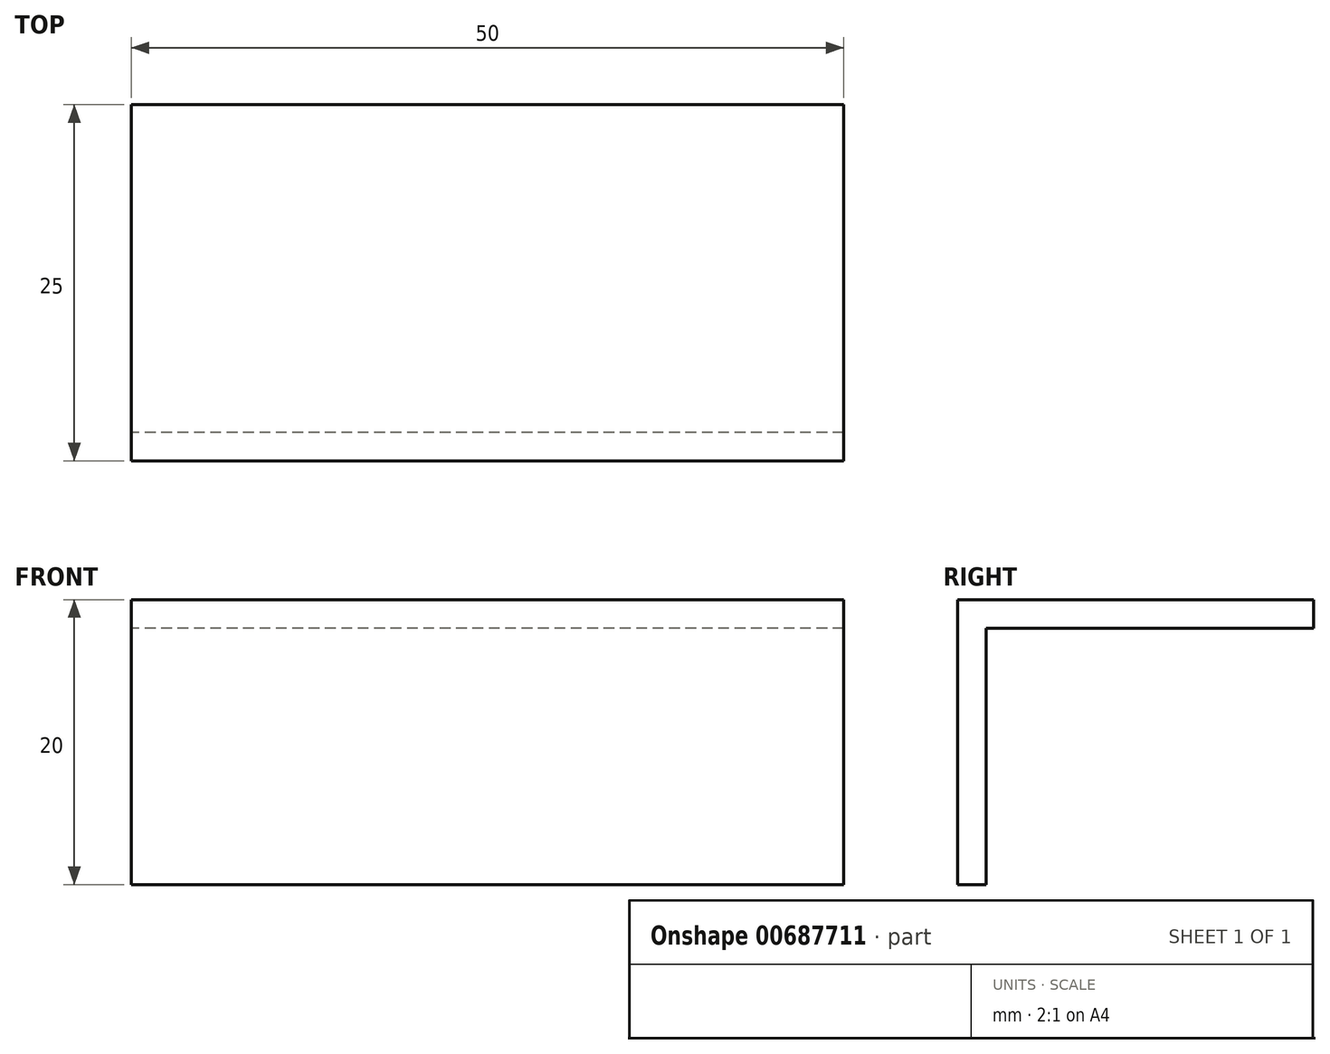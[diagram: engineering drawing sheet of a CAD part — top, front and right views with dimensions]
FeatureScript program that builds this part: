
annotation { "Feature Type Name" : "Feature", "Feature Type Description" : "" }
export const myFeature = defineFeature(function(context is Context, id is Id, definition is map)
    precondition{}
    {
        {
            var Q0;
            Q0=qCreatedBy(makeId("Right.planeOp"),FACE);
            var sketch = newSketch(context, id + "F0", { "sketchPlane" : qUnion([Q0])});
            skLineSegment(sketch, "E0", {"start": v(-25, 1.4) * mm, "end": v(-25, 21.4) * mm});
            skLineSegment(sketch, "E1", {"start": v(-25, 21.4) * mm, "end": v(0, 21.4) * mm});
            skLineSegment(sketch, "E2", {"start": v(0, 21.4) * mm, "end": v(0, 19.4) * mm});
            skLineSegment(sketch, "E3", {"start": v(0, 19.4) * mm, "end": v(-23, 19.4) * mm});
            skLineSegment(sketch, "E4", {"start": v(-23, 19.4) * mm, "end": v(-23, 1.4) * mm});
            skLineSegment(sketch, "E5", {"start": v(-23, 1.4) * mm, "end": v(-25, 1.4) * mm});
            skSolve(sketch);
        }
        {
            var Q0;
            Q0 = qSketchRegion(id + "F0", true);
            extrude(context, id + "F1", {"entities" : qUnion([Q0]), "depth" : 50 * mm, "offsetDistance" : 25 * mm});
        }
    });
